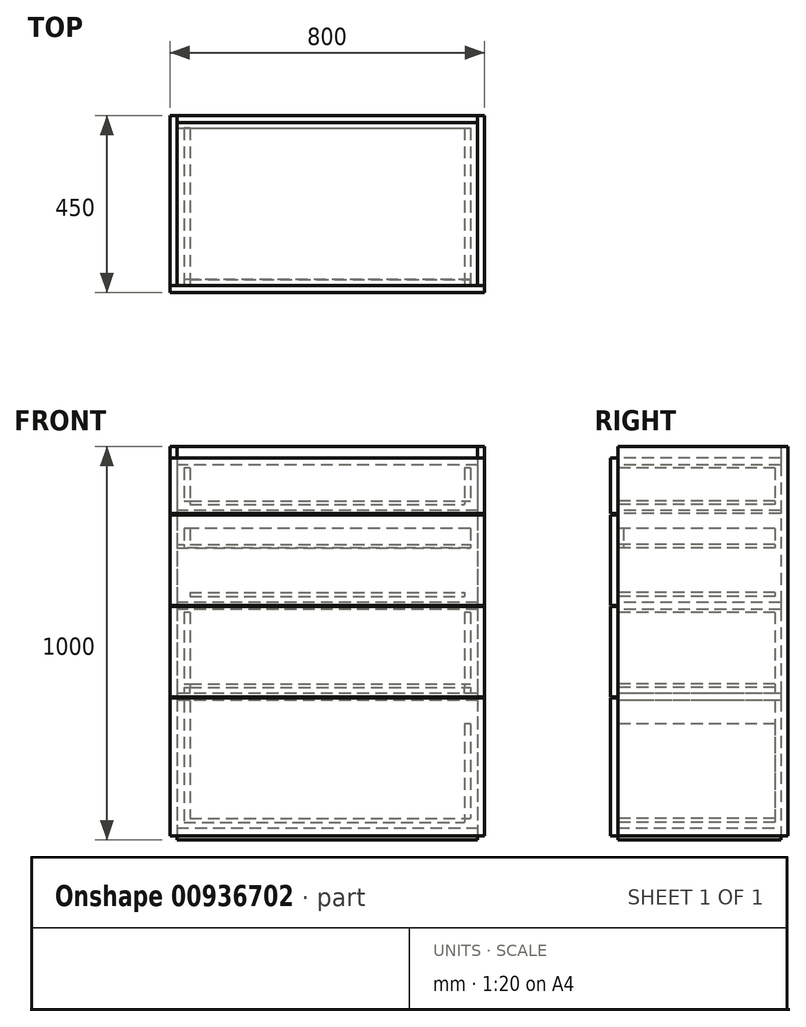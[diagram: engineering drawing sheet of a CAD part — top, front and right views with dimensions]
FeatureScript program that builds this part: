
annotation { "Feature Type Name" : "Feature", "Feature Type Description" : "" }
export const myFeature = defineFeature(function(context is Context, id is Id, definition is map)
    precondition{}
    {
        {
            var Q0;
            Q0=qCreatedBy(makeId("Top.planeOp"),FACE);
            var sketch = newSketch(context, id + "F0", { "sketchPlane" : qUnion([Q0])});
            skLineSegment(sketch, "E0.bottom", {"start": v(0, 0) * mm, "end": v(800, 0) * mm});
            skLineSegment(sketch, "E0.top", {"start": v(0, 432) * mm, "end": v(800, 432) * mm});
            skLineSegment(sketch, "E0.left", {"start": v(0, 0) * mm, "end": v(0, 432) * mm});
            skLineSegment(sketch, "E0.right", {"start": v(800, 0) * mm, "end": v(800, 432) * mm});
            skLineSegment(sketch, "E1.0", {"start": v(18, 0) * mm, "end": v(18, 432) * mm});
            skLineSegment(sketch, "E2", {"start": v(400, 467.89) * mm, "end": v(400, 549.02) * mm, "construction": true});
            skPoint(sketch, "E2.startSnap0", {"position": v(400, 432) * mm});
            skLineSegment(sketch, "E3.MirrorCS", {"start": v(782, 0) * mm, "end": v(782, 432) * mm});
            skLineSegment(sketch, "E4", {"start": v(828.28, 216) * mm, "end": v(900.38, 216) * mm, "construction": true});
            skPoint(sketch, "E4.startSnap0", {"position": v(800, 216) * mm});
            skLineSegment(sketch, "E5.0", {"start": v(0, 414) * mm, "end": v(800, 414) * mm});
            skSolve(sketch);
        }
        {
            var Q0;
            {var subQ0=sQuery(id+"F0.wireOp",EDGE,"E0.left");var subQ1=sQuery(id+"F0.wireOp",EDGE,"E0.bottom");var subQ2=makeQuery(id+"F0.imprint","INTERSECT",VERTEX,{"derivedFrom":[subQ1,subQ0]});Q0=makeQuery(id+"F0.imprint","IMPRINT",FACE,{"disambiguationData":[TD([[makeQuery(id+"F0.imprint","IMPRINT",EDGE,{"disambiguationData":[TD([[subQ2,-1.0]])],"derivedFrom":subQ1}),1.0]])]});}
            var Q1;
            {var subQ0=sQuery(id+"F0.wireOp",EDGE,"E0.left");var subQ1=sQuery(id+"F0.wireOp",EDGE,"E0.top");var subQ2=makeQuery(id+"F0.imprint","INTERSECT",VERTEX,{"derivedFrom":[subQ1,subQ0]});Q1=makeQuery(id+"F0.imprint","IMPRINT",FACE,{"disambiguationData":[TD([[makeQuery(id+"F0.imprint","IMPRINT",EDGE,{"disambiguationData":[TD([[subQ2,-1.0]])],"derivedFrom":subQ1}),-1.0]])]});}
            var Q2;
            {var subQ0=sQuery(id+"F0.wireOp",EDGE,"E0.right");var subQ1=sQuery(id+"F0.wireOp",EDGE,"E0.top");var subQ2=makeQuery(id+"F0.imprint","INTERSECT",VERTEX,{"derivedFrom":[subQ1,subQ0]});Q2=makeQuery(id+"F0.imprint","IMPRINT",FACE,{"disambiguationData":[TD([[makeQuery(id+"F0.imprint","IMPRINT",EDGE,{"disambiguationData":[TD([[subQ2,1.0]])],"derivedFrom":subQ1}),-1.0]])]});}
            var Q3;
            {var subQ0=sQuery(id+"F0.wireOp",EDGE,"E0.right");var subQ1=sQuery(id+"F0.wireOp",EDGE,"E0.bottom");var subQ2=makeQuery(id+"F0.imprint","INTERSECT",VERTEX,{"derivedFrom":[subQ1,subQ0]});Q3=makeQuery(id+"F0.imprint","IMPRINT",FACE,{"disambiguationData":[TD([[makeQuery(id+"F0.imprint","IMPRINT",EDGE,{"disambiguationData":[TD([[subQ2,1.0]])],"derivedFrom":subQ1}),1.0]])]});}
            extrude(context, id + "F1", {"entities" : qUnion([Q0, Q1, Q2, Q3]), "depth" : 990 * mm, "offsetDistance" : 25 * mm});
        }
        {
            var Q0;
            {var subQ0=sQuery(id+"F0.wireOp",EDGE,"E1.0");var subQ1=sQuery(id+"F0.wireOp",EDGE,"E0.top");var subQ2=makeQuery(id+"F0.imprint","INTERSECT",VERTEX,{"derivedFrom":[subQ1,subQ0]});Q0=makeQuery(id+"F0.imprint","IMPRINT",FACE,{"disambiguationData":[TD([[makeQuery(id+"F0.imprint","IMPRINT",EDGE,{"disambiguationData":[TD([[subQ2,-1.0]])],"derivedFrom":subQ1}),-1.0]])]});}
            var Q1;
            Q1=makeQuery(id+"F1.opExtrude","CAP_FACE",FACE,{"disambiguationData":[OSD([sQuery(id+"F0.wireOp",EDGE,"E0.bottom"),sQuery(id+"F0.wireOp",EDGE,"E0.top"),sQuery(id+"F0.wireOp",EDGE,"E0.left"),sQuery(id+"F0.wireOp",EDGE,"E1.0")])],"isStart":false});
            extrude(context, id + "F2", {"entities" : qUnion([Q0]), "endBound" : BoundingType.UP_TO_SURFACE, "depth" : 25 * mm, "endBoundEntityFace" : qUnion([Q1]), "offsetDistance" : 25 * mm});
        }
        {
            var Q0;
            {var subQ0=sQuery(id+"F0.wireOp",EDGE,"E1.0");var subQ1=sQuery(id+"F0.wireOp",EDGE,"E0.bottom");var subQ2=makeQuery(id+"F0.imprint","INTERSECT",VERTEX,{"derivedFrom":[subQ1,subQ0]});Q0=makeQuery(id+"F0.imprint","IMPRINT",FACE,{"disambiguationData":[TD([[makeQuery(id+"F0.imprint","IMPRINT",EDGE,{"disambiguationData":[TD([[subQ2,-1.0]])],"derivedFrom":subQ1}),1.0]])]});}
            extrude(context, id + "F3", {"entities" : qUnion([Q0]), "depth" : 20 * mm, "offsetDistance" : 25 * mm, "hasSecondDirection" : true, "secondDirectionOppositeDirection" : true, "secondDirectionDepth" : 10 * mm});
        }
        {
            var Q0;
            {var subQ0=sQuery(id+"F0.wireOp",EDGE,"E0.bottom");Q0=makeQuery(id+"F1.opExtrude","SWEPT_FACE",FACE,{"disambiguationData":[OSD([subQ0]),TDD([makeQuery(id+"F0.imprint","IMPRINT",EDGE,{"disambiguationData":[TD([[makeQuery(id+"F0.imprint","INTERSECT",VERTEX,{"derivedFrom":[subQ0,sQuery(id+"F0.wireOp",EDGE,"E0.left")]}),-1.0]])],"derivedFrom":subQ0})])]});}
            var sketch = newSketch(context, id + "F4", { "sketchPlane" : qUnion([Q0])});
            skLineSegment(sketch, "E6.bottom", {"start": v(800, 583) * mm, "end": v(603, 583) * mm});
            skLineSegment(sketch, "E6.top", {"start": v(800, 353) * mm, "end": v(603, 353) * mm});
            skLineSegment(sketch, "E6.left", {"start": v(800, 583) * mm, "end": v(800, 353) * mm});
            skLineSegment(sketch, "E6.right", {"start": v(603, 583) * mm, "end": v(603, 353) * mm});
            skLineSegment(sketch, "E7.bottom", {"start": v(600, 583) * mm, "end": v(0, 583) * mm});
            skLineSegment(sketch, "E7.top", {"start": v(600, 353) * mm, "end": v(0, 353) * mm});
            skLineSegment(sketch, "E7.left", {"start": v(600, 583) * mm, "end": v(600, 353) * mm});
            skLineSegment(sketch, "E7.right", {"start": v(0, 583) * mm, "end": v(0, 353) * mm});
            skLineSegment(sketch, "E8", {"start": v(603, 468) * mm, "end": v(600, 468) * mm, "construction": true});
            skLineSegment(sketch, "E9.bottom", {"start": v(0, 350) * mm, "end": v(197, 350) * mm});
            skLineSegment(sketch, "E9.top", {"start": v(0, 0) * mm, "end": v(197, 0) * mm});
            skLineSegment(sketch, "E9.right", {"start": v(197, 350) * mm, "end": v(197, 0) * mm});
            skLineSegment(sketch, "E10.bottom", {"start": v(200, 350) * mm, "end": v(800, 350) * mm});
            skLineSegment(sketch, "E10.top", {"start": v(200, 0) * mm, "end": v(800, 0) * mm});
            skLineSegment(sketch, "E10.left", {"start": v(200, 350) * mm, "end": v(200, 0) * mm});
            skLineSegment(sketch, "E10.right", {"start": v(800, 350) * mm, "end": v(800, 0) * mm});
            skLineSegment(sketch, "E11", {"start": v(10.26, 353) * mm, "end": v(10.26, 350) * mm, "construction": true});
            skLineSegment(sketch, "E12", {"start": v(200, 175) * mm, "end": v(197, 175) * mm, "construction": true});
            skLineSegment(sketch, "E13.bottom", {"start": v(800, 816) * mm, "end": v(200, 816) * mm});
            skLineSegment(sketch, "E13.top", {"start": v(800, 586) * mm, "end": v(200, 586) * mm});
            skLineSegment(sketch, "E13.left", {"start": v(800, 816) * mm, "end": v(800, 586) * mm});
            skLineSegment(sketch, "E13.right", {"start": v(200, 816) * mm, "end": v(200, 586) * mm});
            skLineSegment(sketch, "E14.bottom", {"start": v(197, 816) * mm, "end": v(0, 816) * mm});
            skLineSegment(sketch, "E14.top", {"start": v(197, 586) * mm, "end": v(0, 586) * mm});
            skLineSegment(sketch, "E14.left", {"start": v(197, 816) * mm, "end": v(197, 586) * mm});
            skLineSegment(sketch, "E14.right", {"start": v(0, 816) * mm, "end": v(0, 586) * mm});
            skLineSegment(sketch, "E15", {"start": v(277.64, 586) * mm, "end": v(277.64, 583) * mm, "construction": true});
            skLineSegment(sketch, "E16", {"start": v(200, 654.54) * mm, "end": v(197, 654.54) * mm, "construction": true});
            skLineSegment(sketch, "E17.bottom", {"start": v(0, 990) * mm, "end": v(800, 990) * mm});
            skLineSegment(sketch, "E17.top", {"start": v(0, 819) * mm, "end": v(800, 819) * mm});
            skLineSegment(sketch, "E17.left", {"start": v(0, 990) * mm, "end": v(0, 819) * mm});
            skLineSegment(sketch, "E17.right", {"start": v(800, 990) * mm, "end": v(800, 819) * mm});
            skLineSegment(sketch, "E18", {"start": v(-67.03, 819) * mm, "end": v(-67.03, 816) * mm, "construction": true});
            skLineSegment(sketch, "E19", {"start": v(0, 350) * mm, "end": v(0, 0) * mm});
            skLineSegment(sketch, "E20", {"start": v(0, 960) * mm, "end": v(800, 960) * mm});
            skLineSegment(sketch, "E21", {"start": v(197, 350) * mm, "end": v(200, 350) * mm});
            skLineSegment(sketch, "E22", {"start": v(197, 0) * mm, "end": v(200, 0) * mm});
            skLineSegment(sketch, "E23", {"start": v(600, 353) * mm, "end": v(603, 353) * mm});
            skLineSegment(sketch, "E24", {"start": v(600, 583) * mm, "end": v(603, 583) * mm});
            skLineSegment(sketch, "E25", {"start": v(197, 586) * mm, "end": v(200, 586) * mm});
            skLineSegment(sketch, "E26", {"start": v(197, 816) * mm, "end": v(200, 816) * mm});
            skSolve(sketch);
        }
        {
            var Q0;
            {var subQ0=sQuery(id+"F4.wireOp",EDGE,"E17.right");var subQ1=sQuery(id+"F4.wireOp",EDGE,"E17.top");var subQ2=makeQuery(id+"F4.imprint","INTERSECT",VERTEX,{"derivedFrom":[subQ1,subQ0]});Q0=makeQuery(id+"F4.imprint","IMPRINT",FACE,{"disambiguationData":[TD([[makeQuery(id+"F4.imprint","IMPRINT",EDGE,{"disambiguationData":[TD([[subQ2,1.0]])],"derivedFrom":subQ0}),-1.0]])]});}
            var Q1;
            {var subQ0=sQuery(id+"F4.wireOp",EDGE,"E17.left");var subQ6=sQuery(id+"F4.wireOp",EDGE,"E20");var subQ7=makeQuery(id+"F4.imprint","INTERSECT",VERTEX,{"derivedFrom":[subQ0,subQ6]});Q1=makeQuery(id+"F4.imprint","IMPRINT",FACE,{"disambiguationData":[TD([[makeQuery(id+"F4.imprint","IMPRINT",EDGE,{"disambiguationData":[TD([[subQ7,-1.0]])],"derivedFrom":subQ6}),-1.0]])]});}
            var Q2;
            Q2=makeQuery(id+"F4.imprint","IMPRINT",FACE,{"disambiguationData":[TD([[makeQuery(id+"F4.imprint","IMPRINT",EDGE,{"derivedFrom":sQuery(id+"F4.wireOp",EDGE,"E13.bottom")}),1.0]])]});
            var Q3;
            {var subQ0=sQuery(id+"F4.wireOp",EDGE,"E7.left");Q3=makeQuery(id+"F4.imprint","IMPRINT",FACE,{"disambiguationData":[TD([[makeQuery(id+"F4.imprint","IMPRINT",EDGE,{"derivedFrom":subQ0}),-1.0]])]});}
            var Q4;
            {var subQ0=sQuery(id+"F4.wireOp",EDGE,"E7.right");Q4=makeQuery(id+"F4.imprint","IMPRINT",FACE,{"disambiguationData":[TD([[makeQuery(id+"F4.imprint","IMPRINT",EDGE,{"derivedFrom":subQ0}),1.0]])]});}
            var Q5;
            {var subQ0=sQuery(id+"F4.wireOp",EDGE,"E9.right");Q5=makeQuery(id+"F4.imprint","IMPRINT",FACE,{"disambiguationData":[TD([[makeQuery(id+"F4.imprint","IMPRINT",EDGE,{"derivedFrom":subQ0}),-1.0]])]});}
            var Q6;
            {var subQ0=sQuery(id+"F4.wireOp",EDGE,"E19");Q6=makeQuery(id+"F4.imprint","IMPRINT",FACE,{"disambiguationData":[TD([[makeQuery(id+"F4.imprint","IMPRINT",EDGE,{"derivedFrom":subQ0}),1.0]])]});}
            var Q7;
            Q7=makeQuery(id+"F4.imprint","IMPRINT",FACE,{"disambiguationData":[TD([[makeQuery(id+"F4.imprint","IMPRINT",EDGE,{"derivedFrom":sQuery(id+"F4.wireOp",EDGE,"E10.bottom")}),-1.0]])]});
            var Q8;
            Q8=makeQuery(id+"F4.imprint","IMPRINT",FACE,{"disambiguationData":[TD([[makeQuery(id+"F4.imprint","IMPRINT",EDGE,{"derivedFrom":sQuery(id+"F4.wireOp",EDGE,"E13.right")}),-1.0]])]});
            var Q9;
            {var subQ0=sQuery(id+"F4.wireOp",EDGE,"E14.left");Q9=makeQuery(id+"F4.imprint","IMPRINT",FACE,{"disambiguationData":[TD([[makeQuery(id+"F4.imprint","IMPRINT",EDGE,{"derivedFrom":subQ0}),-1.0]])]});}
            var Q10;
            {var subQ0=sQuery(id+"F4.wireOp",EDGE,"E14.right");Q10=makeQuery(id+"F4.imprint","IMPRINT",FACE,{"disambiguationData":[TD([[makeQuery(id+"F4.imprint","IMPRINT",EDGE,{"derivedFrom":subQ0}),1.0]])]});}
            var Q11;
            Q11=makeQuery(id+"F4.imprint","IMPRINT",FACE,{"disambiguationData":[TD([[makeQuery(id+"F4.imprint","IMPRINT",EDGE,{"derivedFrom":sQuery(id+"F4.wireOp",EDGE,"E6.right")}),-1.0]])]});
            var Q12;
            Q12=makeQuery(id+"F4.imprint","IMPRINT",FACE,{"disambiguationData":[TD([[makeQuery(id+"F4.imprint","IMPRINT",EDGE,{"derivedFrom":sQuery(id+"F4.wireOp",EDGE,"E6.bottom")}),1.0]])]});
            var Q13;
            Q13=makeQuery(id+"F4.imprint","IMPRINT",FACE,{"disambiguationData":[TD([[makeQuery(id+"F4.imprint","IMPRINT",EDGE,{"derivedFrom":sQuery(id+"F4.wireOp",EDGE,"E9.right")}),1.0]])]});
            extrude(context, id + "F5", {"entities" : qUnion([Q0, Q1, Q2, Q3, Q4, Q5, Q6, Q7, Q8, Q9, Q10, Q11, Q12, Q13]), "depth" : 18 * mm, "offsetDistance" : 25 * mm});
        }
        {
            var Q0;
            Q0=makeQuery(id+"F5.opExtrude","CAP_FACE",FACE,{"disambiguationData":[OSD([sQuery(id+"F4.wireOp",EDGE,"E17.top"),sQuery(id+"F4.wireOp",EDGE,"E17.left"),sQuery(id+"F4.wireOp",EDGE,"E17.right"),sQuery(id+"F4.wireOp",EDGE,"E20")])],"isStart":true});
            var sketch = newSketch(context, id + "F6", { "sketchPlane" : qUnion([Q0])});
            skLineSegment(sketch, "E27.bottom", {"start": v(-782, 826.5) * mm, "end": v(-18, 826.5) * mm});
            skLineSegment(sketch, "E27.top", {"start": v(-782, 808.5) * mm, "end": v(-18, 808.5) * mm});
            skLineSegment(sketch, "E27.left", {"start": v(-782, 826.5) * mm, "end": v(-782, 808.5) * mm});
            skLineSegment(sketch, "E27.right", {"start": v(-18, 826.5) * mm, "end": v(-18, 808.5) * mm});
            skPoint(sketch, "E28", {"position": v(-782, 817.5) * mm});
            skLineSegment(sketch, "E29.bottom", {"start": v(-782, 593.5) * mm, "end": v(-18, 593.5) * mm});
            skLineSegment(sketch, "E29.top", {"start": v(-782, 575.5) * mm, "end": v(-18, 575.5) * mm});
            skLineSegment(sketch, "E29.left", {"start": v(-782, 593.5) * mm, "end": v(-782, 575.5) * mm});
            skLineSegment(sketch, "E29.right", {"start": v(-18, 593.5) * mm, "end": v(-18, 575.5) * mm});
            skLineSegment(sketch, "E30.bottom", {"start": v(-782, 361.75) * mm, "end": v(-18, 361.75) * mm});
            skLineSegment(sketch, "E30.top", {"start": v(-782, 343.75) * mm, "end": v(-18, 343.75) * mm});
            skLineSegment(sketch, "E30.left", {"start": v(-782, 361.75) * mm, "end": v(-782, 343.75) * mm});
            skLineSegment(sketch, "E30.right", {"start": v(-18, 361.75) * mm, "end": v(-18, 343.75) * mm});
            skLineSegment(sketch, "E31.bottom", {"start": v(-782, 343.75) * mm, "end": v(-764, 343.75) * mm});
            skLineSegment(sketch, "E31.top", {"start": v(-782, 20) * mm, "end": v(-764, 20) * mm});
            skLineSegment(sketch, "E31.left", {"start": v(-782, 343.75) * mm, "end": v(-782, 20) * mm});
            skLineSegment(sketch, "E31.right", {"start": v(-764, 343.75) * mm, "end": v(-764, 20) * mm});
            skLineSegment(sketch, "E32.bottom", {"start": v(-782, 575.5) * mm, "end": v(-764, 575.5) * mm});
            skLineSegment(sketch, "E32.top", {"start": v(-782, 361.75) * mm, "end": v(-764, 361.75) * mm});
            skLineSegment(sketch, "E32.left", {"start": v(-782, 575.5) * mm, "end": v(-782, 361.75) * mm});
            skLineSegment(sketch, "E32.right", {"start": v(-764, 575.5) * mm, "end": v(-764, 361.75) * mm});
            skLineSegment(sketch, "E33.bottom", {"start": v(-36, 808.5) * mm, "end": v(-18, 808.5) * mm});
            skLineSegment(sketch, "E33.top", {"start": v(-36, 593.5) * mm, "end": v(-18, 593.5) * mm});
            skLineSegment(sketch, "E33.left", {"start": v(-36, 808.5) * mm, "end": v(-36, 593.5) * mm});
            skLineSegment(sketch, "E33.right", {"start": v(-18, 808.5) * mm, "end": v(-18, 593.5) * mm});
            skPoint(sketch, "E34", {"position": v(-782, 584.5) * mm});
            skPoint(sketch, "E35", {"position": v(-782, 352.75) * mm});
            skPoint(sketch, "E36", {"position": v(-773, 343.75) * mm});
            skLineSegment(sketch, "E37.bottom", {"start": v(-782, 960) * mm, "end": v(-18, 960) * mm});
            skLineSegment(sketch, "E37.top", {"start": v(-782, 942) * mm, "end": v(-18, 942) * mm});
            skLineSegment(sketch, "E37.left", {"start": v(-782, 960) * mm, "end": v(-782, 942) * mm});
            skLineSegment(sketch, "E37.right", {"start": v(-18, 960) * mm, "end": v(-18, 942) * mm});
            skLineSegment(sketch, "E38.bottom", {"start": v(-782, 808.5) * mm, "end": v(-764, 808.5) * mm});
            skLineSegment(sketch, "E38.top", {"start": v(-782, 593.5) * mm, "end": v(-764, 593.5) * mm});
            skLineSegment(sketch, "E38.left", {"start": v(-782, 808.5) * mm, "end": v(-782, 593.5) * mm});
            skLineSegment(sketch, "E38.right", {"start": v(-764, 808.5) * mm, "end": v(-764, 593.5) * mm});
            skLineSegment(sketch, "E39.bottom", {"start": v(-18, 343.75) * mm, "end": v(-36, 343.75) * mm});
            skLineSegment(sketch, "E39.top", {"start": v(-18, 20) * mm, "end": v(-36, 20) * mm});
            skLineSegment(sketch, "E39.left", {"start": v(-18, 343.75) * mm, "end": v(-18, 20) * mm});
            skLineSegment(sketch, "E39.right", {"start": v(-36, 343.75) * mm, "end": v(-36, 20) * mm});
            skLineSegment(sketch, "E40.bottom", {"start": v(-18, 575.5) * mm, "end": v(-36, 575.5) * mm});
            skLineSegment(sketch, "E40.top", {"start": v(-18, 361.75) * mm, "end": v(-36, 361.75) * mm});
            skLineSegment(sketch, "E40.left", {"start": v(-18, 575.5) * mm, "end": v(-18, 361.75) * mm});
            skLineSegment(sketch, "E40.right", {"start": v(-36, 575.5) * mm, "end": v(-36, 361.75) * mm});
            skLineSegment(sketch, "E41.bottom", {"start": v(-18, 942) * mm, "end": v(-36, 942) * mm});
            skLineSegment(sketch, "E41.top", {"start": v(-18, 826.5) * mm, "end": v(-36, 826.5) * mm});
            skLineSegment(sketch, "E41.left", {"start": v(-18, 942) * mm, "end": v(-18, 826.5) * mm});
            skLineSegment(sketch, "E41.right", {"start": v(-36, 942) * mm, "end": v(-36, 826.5) * mm});
            skLineSegment(sketch, "E42.bottom", {"start": v(-782, 942) * mm, "end": v(-764, 942) * mm});
            skLineSegment(sketch, "E42.top", {"start": v(-782, 826.5) * mm, "end": v(-764, 826.5) * mm});
            skLineSegment(sketch, "E42.left", {"start": v(-782, 942) * mm, "end": v(-782, 826.5) * mm});
            skLineSegment(sketch, "E42.right", {"start": v(-764, 942) * mm, "end": v(-764, 826.5) * mm});
            skLineSegment(sketch, "E43.bottom", {"start": v(-36, 841.5) * mm, "end": v(-764, 841.5) * mm});
            skLineSegment(sketch, "E43.top", {"start": v(-36, 851.5) * mm, "end": v(-764, 851.5) * mm});
            skLineSegment(sketch, "E43.left", {"start": v(-36, 841.5) * mm, "end": v(-36, 851.5) * mm});
            skLineSegment(sketch, "E43.right", {"start": v(-764, 841.5) * mm, "end": v(-764, 851.5) * mm});
            skLineSegment(sketch, "E44", {"start": v(-36, 841.5) * mm, "end": v(-18, 841.5) * mm});
            skLineSegment(sketch, "E45", {"start": v(-764, 841.5) * mm, "end": v(-782, 841.5) * mm});
            skLineSegment(sketch, "E46.bottom", {"start": v(-36, 608.5) * mm, "end": v(-764, 608.5) * mm});
            skLineSegment(sketch, "E46.top", {"start": v(-36, 618.5) * mm, "end": v(-764, 618.5) * mm});
            skLineSegment(sketch, "E46.left", {"start": v(-36, 608.5) * mm, "end": v(-36, 618.5) * mm});
            skLineSegment(sketch, "E46.right", {"start": v(-764, 608.5) * mm, "end": v(-764, 618.5) * mm});
            skLineSegment(sketch, "E47.bottom", {"start": v(-36, 376.75) * mm, "end": v(-764, 376.75) * mm});
            skLineSegment(sketch, "E47.top", {"start": v(-36, 386.75) * mm, "end": v(-764, 386.75) * mm});
            skLineSegment(sketch, "E47.left", {"start": v(-36, 376.75) * mm, "end": v(-36, 386.75) * mm});
            skLineSegment(sketch, "E47.right", {"start": v(-764, 376.75) * mm, "end": v(-764, 386.75) * mm});
            skLineSegment(sketch, "E48.bottom", {"start": v(-36, 35) * mm, "end": v(-764, 35) * mm});
            skLineSegment(sketch, "E48.top", {"start": v(-36, 45) * mm, "end": v(-764, 45) * mm});
            skLineSegment(sketch, "E48.left", {"start": v(-36, 35) * mm, "end": v(-36, 45) * mm});
            skLineSegment(sketch, "E48.right", {"start": v(-764, 35) * mm, "end": v(-764, 45) * mm});
            skLineSegment(sketch, "E49", {"start": v(-36, 608.5) * mm, "end": v(-18, 608.5) * mm});
            skLineSegment(sketch, "E50", {"start": v(-36, 376.75) * mm, "end": v(-18, 376.75) * mm});
            skLineSegment(sketch, "E51", {"start": v(-36, 35) * mm, "end": v(-18, 35) * mm});
            skLineSegment(sketch, "E52", {"start": v(-764, 376.75) * mm, "end": v(-782, 376.75) * mm});
            skLineSegment(sketch, "E53", {"start": v(-764, 608.5) * mm, "end": v(-782, 608.5) * mm});
            skLineSegment(sketch, "E54", {"start": v(-764, 35) * mm, "end": v(-782, 35) * mm});
            skLineSegment(sketch, "E55", {"start": v(-525.16, 608.5) * mm, "end": v(-525.16, 593.5) * mm, "construction": true});
            skLineSegment(sketch, "E56", {"start": v(-525.16, 376.75) * mm, "end": v(-525.16, 361.75) * mm, "construction": true});
            skLineSegment(sketch, "E57", {"start": v(-538.6, 35) * mm, "end": v(-538.6, 20) * mm, "construction": true});
            skLineSegment(sketch, "E58", {"start": v(-520.69, 841.5) * mm, "end": v(-520.69, 826.5) * mm, "construction": true});
            skLineSegment(sketch, "E59.bottom", {"start": v(-18, 781) * mm, "end": v(-764, 781) * mm});
            skLineSegment(sketch, "E59.top", {"start": v(-18, 731) * mm, "end": v(-764, 731) * mm});
            skLineSegment(sketch, "E59.left", {"start": v(-18, 781) * mm, "end": v(-18, 731) * mm});
            skLineSegment(sketch, "E59.right", {"start": v(-764, 781) * mm, "end": v(-764, 731) * mm});
            skLineSegment(sketch, "E60.0", {"start": v(-51, 934.5) * mm, "end": v(-51, 841.5) * mm});
            skLineSegment(sketch, "E61.0", {"start": v(-51, 808.5) * mm, "end": v(-51, 593.5) * mm});
            skLineSegment(sketch, "E62.0", {"start": v(-51, 575.5) * mm, "end": v(-51, 376.75) * mm});
            skLineSegment(sketch, "E63.0", {"start": v(-51, 285) * mm, "end": v(-51, 35) * mm});
            skLineSegment(sketch, "E64.0", {"start": v(-749, 285) * mm, "end": v(-749, 35) * mm});
            skLineSegment(sketch, "E65.0", {"start": v(-749, 568) * mm, "end": v(-749, 376.75) * mm});
            skLineSegment(sketch, "E66.0", {"start": v(-749, 808.5) * mm, "end": v(-749, 593.5) * mm});
            skLineSegment(sketch, "E67.0", {"start": v(-749, 942) * mm, "end": v(-749, 841.5) * mm});
            skLineSegment(sketch, "E68.0", {"start": v(-782, 934.5) * mm, "end": v(-18, 934.5) * mm});
            skLineSegment(sketch, "E69", {"start": v(-764, 285) * mm, "end": v(-749, 285) * mm});
            skLineSegment(sketch, "E70", {"start": v(-51, 285) * mm, "end": v(-36, 285) * mm});
            skLineSegment(sketch, "E71.0", {"start": v(-18, 741) * mm, "end": v(-764, 741) * mm});
            skLineSegment(sketch, "E72.0", {"start": v(-782, 568) * mm, "end": v(-18, 568) * mm});
            skLineSegment(sketch, "E73.0", {"start": v(-782, 801) * mm, "end": v(-18, 801) * mm});
            skLineSegment(sketch, "E74", {"start": v(-826.43, 586) * mm, "end": v(-826.43, 583) * mm, "construction": true});
            skPoint(sketch, "E75", {"position": v(-826.43, 584.5) * mm});
            skLineSegment(sketch, "E76", {"start": v(-818.28, 819) * mm, "end": v(-818.28, 816) * mm, "construction": true});
            skPoint(sketch, "E77", {"position": v(-818.28, 817.5) * mm});
            skLineSegment(sketch, "E78", {"start": v(-749, 285) * mm, "end": v(-749, 781) * mm});
            skLineSegment(sketch, "E79", {"start": v(-51, 285) * mm, "end": v(-51, 781) * mm});
            skLineSegment(sketch, "E80.0", {"start": v(-18, 711) * mm, "end": v(-764, 711) * mm});
            skSolve(sketch);
        }
        {
            var Q0;
            Q0=makeQuery(id+"F6.imprint","IMPRINT",FACE,{"disambiguationData":[TD([[makeQuery(id+"F6.imprint","IMPRINT",EDGE,{"derivedFrom":sQuery(id+"F6.wireOp",EDGE,"E37.bottom")}),1.0]])]});
            var Q1;
            {var subQ6=sQuery(id+"F6.wireOp",EDGE,"ydlJWMBd-Ox5o-gqpe-Jfhi-dBwXmHUTcuoJ.bottom");Q1=makeQuery(id+"F6.imprint","IMPRINT",FACE,{"disambiguationData":[TD([[makeQuery(id+"F6.imprint","IMPRINT",EDGE,{"derivedFrom":subQ6}),1.0]])]});}
            var Q2;
            {var subQ0=sQuery(id+"F6.wireOp",EDGE,"E27.bottom");Q2=makeQuery(id+"F6.imprint","IMPRINT",FACE,{"disambiguationData":[TD([[makeQuery(id+"F6.imprint","IMPRINT",EDGE,{"derivedFrom":subQ0}),-1.0]])]});}
            var Q3;
            {var subQ4=sQuery(id+"F6.wireOp",EDGE,"E29.left");Q3=makeQuery(id+"F6.imprint","IMPRINT",FACE,{"disambiguationData":[TD([[makeQuery(id+"F6.imprint","IMPRINT",EDGE,{"derivedFrom":subQ4}),1.0]])]});}
            var Q4;
            {var subQ3=sQuery(id+"F6.wireOp",EDGE,"E30.left");Q4=makeQuery(id+"F6.imprint","IMPRINT",FACE,{"disambiguationData":[TD([[makeQuery(id+"F6.imprint","IMPRINT",EDGE,{"derivedFrom":subQ3}),1.0]])]});}
            var Q5;
            {var subQ4=sQuery(id+"F6.wireOp",EDGE,"E33.bottom");Q5=makeQuery(id+"F6.imprint","IMPRINT",FACE,{"disambiguationData":[TD([[makeQuery(id+"F6.imprint","IMPRINT",EDGE,{"derivedFrom":subQ4}),1.0]])]});}
            var Q6;
            {var subQ0=sQuery(id+"F6.wireOp",EDGE,"E78");var subQ1=sQuery(id+"F6.wireOp",EDGE,"E29.bottom");var subQ2=makeQuery(id+"F6.imprint","INTERSECT",VERTEX,{"derivedFrom":[subQ1,subQ0]});Q6=makeQuery(id+"F6.imprint","IMPRINT",FACE,{"disambiguationData":[TD([[makeQuery(id+"F6.imprint","IMPRINT",EDGE,{"disambiguationData":[TD([[subQ2,-1.0]])],"derivedFrom":subQ1}),-1.0]])]});}
            var Q7;
            Q7=makeQuery(id+"F6.imprint","IMPRINT",FACE,{"disambiguationData":[TD([[makeQuery(id+"F6.imprint","IMPRINT",EDGE,{"derivedFrom":sQuery(id+"F6.wireOp",EDGE,"E29.right")}),-1.0]])]});
            var Q8;
            {var subQ0=sQuery(id+"F6.wireOp",EDGE,"E78");var subQ1=sQuery(id+"F6.wireOp",EDGE,"E30.bottom");var subQ2=makeQuery(id+"F6.imprint","INTERSECT",VERTEX,{"derivedFrom":[subQ1,subQ0]});Q8=makeQuery(id+"F6.imprint","IMPRINT",FACE,{"disambiguationData":[TD([[makeQuery(id+"F6.imprint","IMPRINT",EDGE,{"disambiguationData":[TD([[subQ2,-1.0]])],"derivedFrom":subQ1}),-1.0]])]});}
            var Q9;
            Q9=makeQuery(id+"F6.imprint","IMPRINT",FACE,{"disambiguationData":[TD([[makeQuery(id+"F6.imprint","IMPRINT",EDGE,{"derivedFrom":sQuery(id+"F6.wireOp",EDGE,"E30.right")}),-1.0]])]});
            var Q10;
            Q10=makeQuery(id+"F2.opExtrude","SWEPT_FACE",FACE,{"disambiguationData":[OSD([sQuery(id+"F0.wireOp",EDGE,"E5.0")])]});
            extrude(context, id + "F7", {"entities" : qUnion([Q0, Q1, Q2, Q3, Q4, Q5, Q6, Q7, Q8, Q9]), "endBound" : BoundingType.UP_TO_SURFACE, "depth" : 25 * mm, "endBoundEntityFace" : qUnion([Q10]), "offsetDistance" : 25 * mm});
        }
        {
            var Q0;
            {var subQ0=sQuery(id+"F6.wireOp",EDGE,"E43.right");Q0=makeQuery(id+"F6.imprint","IMPRINT",FACE,{"disambiguationData":[TD([[makeQuery(id+"F6.imprint","IMPRINT",EDGE,{"derivedFrom":subQ0}),-1.0]])]});}
            var Q1;
            {var subQ0=sQuery(id+"F6.wireOp",EDGE,"E60.0");var subQ1=sQuery(id+"F6.wireOp",EDGE,"E43.bottom");var subQ2=makeQuery(id+"F6.imprint","INTERSECT",VERTEX,{"derivedFrom":[subQ1,subQ0]});Q1=makeQuery(id+"F6.imprint","IMPRINT",FACE,{"disambiguationData":[TD([[makeQuery(id+"F6.imprint","IMPRINT",EDGE,{"disambiguationData":[TD([[subQ2,-1.0]])],"derivedFrom":subQ1}),-1.0]])]});}
            var Q2;
            {var subQ0=sQuery(id+"F6.wireOp",EDGE,"E43.left");Q2=makeQuery(id+"F6.imprint","IMPRINT",FACE,{"disambiguationData":[TD([[makeQuery(id+"F6.imprint","IMPRINT",EDGE,{"derivedFrom":subQ0}),1.0]])]});}
            var Q3;
            {var subQ0=sQuery(id+"F6.wireOp",EDGE,"E46.right");Q3=makeQuery(id+"F6.imprint","IMPRINT",FACE,{"disambiguationData":[TD([[makeQuery(id+"F6.imprint","IMPRINT",EDGE,{"derivedFrom":subQ0}),-1.0]])]});}
            var Q4;
            {var subQ0=sQuery(id+"F6.wireOp",EDGE,"E61.0");var subQ1=sQuery(id+"F6.wireOp",EDGE,"E46.bottom");var subQ2=makeQuery(id+"F6.imprint","INTERSECT",VERTEX,{"derivedFrom":[subQ1,subQ0]});Q4=makeQuery(id+"F6.imprint","IMPRINT",FACE,{"disambiguationData":[TD([[makeQuery(id+"F6.imprint","IMPRINT",EDGE,{"disambiguationData":[TD([[subQ2,-1.0]])],"derivedFrom":subQ1}),-1.0]])]});}
            var Q5;
            {var subQ0=sQuery(id+"F6.wireOp",EDGE,"E46.left");Q5=makeQuery(id+"F6.imprint","IMPRINT",FACE,{"disambiguationData":[TD([[makeQuery(id+"F6.imprint","IMPRINT",EDGE,{"derivedFrom":subQ0}),1.0]])]});}
            var Q6;
            {var subQ0=sQuery(id+"F6.wireOp",EDGE,"E47.right");Q6=makeQuery(id+"F6.imprint","IMPRINT",FACE,{"disambiguationData":[TD([[makeQuery(id+"F6.imprint","IMPRINT",EDGE,{"derivedFrom":subQ0}),-1.0]])]});}
            var Q7;
            {var subQ0=sQuery(id+"F6.wireOp",EDGE,"E62.0");var subQ1=sQuery(id+"F6.wireOp",EDGE,"E47.bottom");var subQ2=makeQuery(id+"F6.imprint","INTERSECT",VERTEX,{"derivedFrom":[subQ1,subQ0]});Q7=makeQuery(id+"F6.imprint","IMPRINT",FACE,{"disambiguationData":[TD([[makeQuery(id+"F6.imprint","IMPRINT",EDGE,{"disambiguationData":[TD([[subQ2,-1.0]])],"derivedFrom":subQ1}),-1.0]])]});}
            var Q8;
            {var subQ0=sQuery(id+"F6.wireOp",EDGE,"E47.left");Q8=makeQuery(id+"F6.imprint","IMPRINT",FACE,{"disambiguationData":[TD([[makeQuery(id+"F6.imprint","IMPRINT",EDGE,{"derivedFrom":subQ0}),1.0]])]});}
            var Q9;
            {var subQ0=sQuery(id+"F6.wireOp",EDGE,"E48.right");Q9=makeQuery(id+"F6.imprint","IMPRINT",FACE,{"disambiguationData":[TD([[makeQuery(id+"F6.imprint","IMPRINT",EDGE,{"derivedFrom":subQ0}),-1.0]])]});}
            var Q10;
            {var subQ0=sQuery(id+"F6.wireOp",EDGE,"E63.0");var subQ1=sQuery(id+"F6.wireOp",EDGE,"E48.bottom");var subQ2=makeQuery(id+"F6.imprint","INTERSECT",VERTEX,{"derivedFrom":[subQ1,subQ0]});Q10=makeQuery(id+"F6.imprint","IMPRINT",FACE,{"disambiguationData":[TD([[makeQuery(id+"F6.imprint","IMPRINT",EDGE,{"disambiguationData":[TD([[subQ2,-1.0]])],"derivedFrom":subQ1}),-1.0]])]});}
            var Q11;
            {var subQ0=sQuery(id+"F6.wireOp",EDGE,"E48.left");Q11=makeQuery(id+"F6.imprint","IMPRINT",FACE,{"disambiguationData":[TD([[makeQuery(id+"F6.imprint","IMPRINT",EDGE,{"derivedFrom":subQ0}),1.0]])]});}
            var Q12;
            {var subQ3=sQuery(id+"F6.wireOp",EDGE,"E69");Q12=makeQuery(id+"F6.imprint","IMPRINT",FACE,{"disambiguationData":[TD([[makeQuery(id+"F6.imprint","IMPRINT",EDGE,{"derivedFrom":subQ3}),-1.0]])]});}
            var Q13;
            {var subQ3=sQuery(id+"F6.wireOp",EDGE,"E70");Q13=makeQuery(id+"F6.imprint","IMPRINT",FACE,{"disambiguationData":[TD([[makeQuery(id+"F6.imprint","IMPRINT",EDGE,{"derivedFrom":subQ3}),-1.0]])]});}
            var Q14;
            {var subQ0=sQuery(id+"F6.wireOp",EDGE,"E59.right");Q14=makeQuery(id+"F6.imprint","IMPRINT",FACE,{"disambiguationData":[TD([[makeQuery(id+"F6.imprint","IMPRINT",EDGE,{"derivedFrom":subQ0}),1.0]])]});}
            var Q15;
            {var subQ0=sQuery(id+"F6.wireOp",EDGE,"E59.bottom");var subQ1=sQuery(id+"F6.wireOp",EDGE,"E39.right");var subQ2=makeQuery(id+"F6.imprint","INTERSECT",VERTEX,{"derivedFrom":[subQ1,subQ0]});Q15=makeQuery(id+"F6.imprint","IMPRINT",FACE,{"disambiguationData":[TD([[makeQuery(id+"F6.imprint","IMPRINT",EDGE,{"disambiguationData":[TD([[subQ2,-1.0]])],"derivedFrom":subQ1}),-1.0]])]});}
            var Q16;
            {var subQ0=sQuery(id+"F6.wireOp",EDGE,"E43.top");var subQ5=sQuery(id+"F6.wireOp",EDGE,"E67.0");var subQ6=makeQuery(id+"F6.imprint","INTERSECT",VERTEX,{"derivedFrom":[subQ0,subQ5]});Q16=makeQuery(id+"F6.imprint","IMPRINT",FACE,{"disambiguationData":[TD([[makeQuery(id+"F6.imprint","IMPRINT",EDGE,{"disambiguationData":[TD([[subQ6,1.0]])],"derivedFrom":subQ5}),-1.0]])]});}
            var Q17;
            {var subQ0=sQuery(id+"F6.wireOp",EDGE,"E43.top");var subQ5=sQuery(id+"F6.wireOp",EDGE,"E60.0");var subQ6=makeQuery(id+"F6.imprint","INTERSECT",VERTEX,{"derivedFrom":[subQ0,subQ5]});Q17=makeQuery(id+"F6.imprint","IMPRINT",FACE,{"disambiguationData":[TD([[makeQuery(id+"F6.imprint","IMPRINT",EDGE,{"disambiguationData":[TD([[subQ6,1.0]])],"derivedFrom":subQ5}),1.0]])]});}
            var Q18;
            {var subQ0=sQuery(id+"F6.wireOp",EDGE,"E63.0");var subQ1=sQuery(id+"F6.wireOp",EDGE,"E59.top");var subQ2=makeQuery(id+"F6.imprint","INTERSECT",VERTEX,{"derivedFrom":[subQ1,subQ0]});Q18=makeQuery(id+"F6.imprint","IMPRINT",FACE,{"disambiguationData":[TD([[makeQuery(id+"F6.imprint","IMPRINT",EDGE,{"disambiguationData":[TD([[subQ2,-1.0]])],"derivedFrom":subQ1}),-1.0]])]});}
            var Q19;
            {var subQ0=sQuery(id+"F6.wireOp",EDGE,"E71.0");var subQ1=sQuery(id+"F6.wireOp",EDGE,"E39.right");var subQ2=makeQuery(id+"F6.imprint","INTERSECT",VERTEX,{"derivedFrom":[subQ1,subQ0]});Q19=makeQuery(id+"F6.imprint","IMPRINT",FACE,{"disambiguationData":[TD([[makeQuery(id+"F6.imprint","IMPRINT",EDGE,{"disambiguationData":[TD([[subQ2,-1.0]])],"derivedFrom":subQ1}),-1.0]])]});}
            var Q20;
            {var subQ0=sQuery(id+"F6.wireOp",EDGE,"E47.top");var subQ5=sQuery(id+"F6.wireOp",EDGE,"E65.0");var subQ6=makeQuery(id+"F6.imprint","INTERSECT",VERTEX,{"derivedFrom":[subQ0,subQ5]});Q20=makeQuery(id+"F6.imprint","IMPRINT",FACE,{"disambiguationData":[TD([[makeQuery(id+"F6.imprint","IMPRINT",EDGE,{"disambiguationData":[TD([[subQ6,1.0]])],"derivedFrom":subQ5}),-1.0]])]});}
            var Q21;
            {var subQ0=sQuery(id+"F6.wireOp",EDGE,"E47.top");var subQ5=sQuery(id+"F6.wireOp",EDGE,"E62.0");var subQ6=makeQuery(id+"F6.imprint","INTERSECT",VERTEX,{"derivedFrom":[subQ0,subQ5]});Q21=makeQuery(id+"F6.imprint","IMPRINT",FACE,{"disambiguationData":[TD([[makeQuery(id+"F6.imprint","IMPRINT",EDGE,{"disambiguationData":[TD([[subQ6,1.0]])],"derivedFrom":subQ5}),1.0]])]});}
            var Q22;
            {var subQ0=sQuery(id+"F6.wireOp",EDGE,"E59.bottom");var subQ1=sQuery(id+"F6.wireOp",EDGE,"E33.left");var subQ2=makeQuery(id+"F6.imprint","INTERSECT",VERTEX,{"derivedFrom":[subQ1,subQ0]});Q22=makeQuery(id+"F6.imprint","IMPRINT",FACE,{"disambiguationData":[TD([[makeQuery(id+"F6.imprint","IMPRINT",EDGE,{"disambiguationData":[TD([[subQ2,-1.0]])],"derivedFrom":subQ1}),-1.0]])]});}
            var Q23;
            {var subQ1=sQuery(id+"F6.wireOp",EDGE,"E32.right");var subQ3=sQuery(id+"F6.wireOp",EDGE,"E72.0");var subQ4=makeQuery(id+"F6.imprint","INTERSECT",VERTEX,{"derivedFrom":[subQ1,subQ3]});Q23=makeQuery(id+"F6.imprint","IMPRINT",FACE,{"disambiguationData":[TD([[makeQuery(id+"F6.imprint","IMPRINT",EDGE,{"disambiguationData":[TD([[subQ4,-1.0]])],"derivedFrom":subQ3}),-1.0]])]});}
            var Q24;
            {var subQ1=sQuery(id+"F6.wireOp",EDGE,"E40.right");var subQ3=sQuery(id+"F6.wireOp",EDGE,"E72.0");var subQ4=makeQuery(id+"F6.imprint","INTERSECT",VERTEX,{"derivedFrom":[subQ1,subQ3]});Q24=makeQuery(id+"F6.imprint","IMPRINT",FACE,{"disambiguationData":[TD([[makeQuery(id+"F6.imprint","IMPRINT",EDGE,{"disambiguationData":[TD([[subQ4,1.0]])],"derivedFrom":subQ3}),-1.0]])]});}
            var Q25;
            {var subQ0=sQuery(id+"F6.wireOp",EDGE,"E46.top");var subQ5=sQuery(id+"F6.wireOp",EDGE,"E78");var subQ6=makeQuery(id+"F6.imprint","INTERSECT",VERTEX,{"derivedFrom":[subQ0,subQ5]});Q25=makeQuery(id+"F6.imprint","IMPRINT",FACE,{"disambiguationData":[TD([[makeQuery(id+"F6.imprint","IMPRINT",EDGE,{"disambiguationData":[TD([[subQ6,-1.0]])],"derivedFrom":subQ5}),1.0]])]});}
            var Q26;
            {var subQ0=sQuery(id+"F6.wireOp",EDGE,"E46.top");var subQ5=sQuery(id+"F6.wireOp",EDGE,"E79");var subQ6=makeQuery(id+"F6.imprint","INTERSECT",VERTEX,{"derivedFrom":[subQ0,subQ5]});Q26=makeQuery(id+"F6.imprint","IMPRINT",FACE,{"disambiguationData":[TD([[makeQuery(id+"F6.imprint","IMPRINT",EDGE,{"disambiguationData":[TD([[subQ6,-1.0]])],"derivedFrom":subQ5}),-1.0]])]});}
            extrude(context, id + "F8", {"entities" : qUnion([Q0, Q1, Q2, Q3, Q4, Q5, Q6, Q7, Q8, Q9, Q10, Q11, Q12, Q13, Q14, Q15, Q16, Q17, Q18, Q19, Q20, Q21, Q22, Q23, Q24, Q25, Q26]), "depth" : 400 * mm, "offsetDistance" : 25 * mm});
        }
        {
            var Q0;
            Q0=makeQuery(id+"F8.opExtrude","SWEPT_FACE",FACE,{"disambiguationData":[OSD([sQuery(id+"F6.wireOp",EDGE,"E71.0")])]});
            var sketch = newSketch(context, id + "F9", { "sketchPlane" : qUnion([Q0])});
            skLineSegment(sketch, "E81.bottom", {"start": v(36, 0) * mm, "end": v(764, 0) * mm});
            skLineSegment(sketch, "E81.top", {"start": v(36, 15) * mm, "end": v(764, 15) * mm});
            skLineSegment(sketch, "E81.left", {"start": v(36, 0) * mm, "end": v(36, 15) * mm});
            skLineSegment(sketch, "E81.right", {"start": v(764, 0) * mm, "end": v(764, 15) * mm});
            skSolve(sketch);
        }
        {
            var Q0;
            {var subQ3=sQuery(id+"F9.wireOp",EDGE,"E81.left");Q0=makeQuery(id+"F9.imprint","IMPRINT",FACE,{"disambiguationData":[TD([[makeQuery(id+"F9.imprint","IMPRINT",EDGE,{"derivedFrom":subQ3}),-1.0]])]});}
            var Q1;
            {var subQ0=sQuery(id+"F9.wireOp",EDGE,"E81.bottom");var subQ1=sQuery(id+"F6.wireOp",EDGE,"E71.0");var subQ2=makeQuery(id+"F8.opExtrude","SWEPT_EDGE",EDGE,{"disambiguationData":[OSD([sQuery(id+"F6.wireOp",EDGE,"E63.0"),subQ1])]});var subQ3=makeQuery(id+"F9.imprint","INTERSECT",VERTEX,{"derivedFrom":[subQ2,subQ0]});Q1=makeQuery(id+"F9.imprint","IMPRINT",FACE,{"disambiguationData":[TD([[makeQuery(id+"F9.imprint","IMPRINT",EDGE,{"disambiguationData":[TD([[subQ3,-1.0]])],"derivedFrom":subQ0}),1.0]])]});}
            var Q2;
            {var subQ3=sQuery(id+"F9.wireOp",EDGE,"E81.right");Q2=makeQuery(id+"F9.imprint","IMPRINT",FACE,{"disambiguationData":[TD([[makeQuery(id+"F9.imprint","IMPRINT",EDGE,{"derivedFrom":subQ3}),1.0]])]});}
            var Q3;
            {var subQ0=sQuery(id+"F6.wireOp",EDGE,"E59.bottom");Q3=makeQuery(id+"F8.opExtrude","SWEPT_FACE",FACE,{"disambiguationData":[OSD([subQ0]),TDD([makeQuery(id+"F6.imprint","IMPRINT",EDGE,{"disambiguationData":[TD([[makeQuery(id+"F6.imprint","INTERSECT",VERTEX,{"derivedFrom":[sQuery(id+"F6.wireOp",EDGE,"E38.right"),subQ0,sQuery(id+"F6.wireOp",EDGE,"E59.right")]}),1.0]])],"derivedFrom":subQ0})])]});}
            var Q4;
            Q4=makeQuery(id+"F8.opExtrude","SWEPT_FACE",FACE,{"disambiguationData":[OSD([sQuery(id+"F6.wireOp",EDGE,"E59.top")])]});
            extrude(context, id + "F10", {"entities" : qUnion([Q0, Q1, Q2]), "endBound" : BoundingType.UP_TO_SURFACE, "depth" : 25 * mm, "endBoundEntityFace" : qUnion([Q3]), "offsetDistance" : 25 * mm, "hasSecondDirection" : true, "secondDirectionBound" : SecondDirectionBoundingType.UP_TO_SURFACE, "secondDirectionOppositeDirection" : true, "secondDirectionDepth" : 25 * mm, "secondDirectionBoundEntityFace" : qUnion([Q4])});
        }
        {
            var Q0;
            Q0=makeQuery(id+"F10.opExtrude","SWEPT_BODY",BODY,{"disambiguationData":[OSD([sQuery(id+"F9.wireOp",EDGE,"E81.bottom"),sQuery(id+"F9.wireOp",EDGE,"E81.top"),sQuery(id+"F9.wireOp",EDGE,"E81.left"),sQuery(id+"F9.wireOp",EDGE,"E81.right")])]});
            var Q1;
            Q1=makeQuery(id+"F8.opExtrude","SWEPT_BODY",BODY,{"disambiguationData":[OSD([sQuery(id+"F6.wireOp",EDGE,"E39.right"),sQuery(id+"F6.wireOp",EDGE,"E59.bottom"),sQuery(id+"F6.wireOp",EDGE,"E59.top"),sQuery(id+"F6.wireOp",EDGE,"E59.right"),sQuery(id+"F6.wireOp",EDGE,"E63.0"),sQuery(id+"F6.wireOp",EDGE,"E64.0"),sQuery(id+"F6.wireOp",EDGE,"E71.0")])]});
            booleanBodies(context, id + "F11", {"operationType" : BooleanOperationType.SUBTRACTION, "tools" : qUnion([Q0]), "targets" : qUnion([Q1]), "keepTools" : true});
        }
    });
